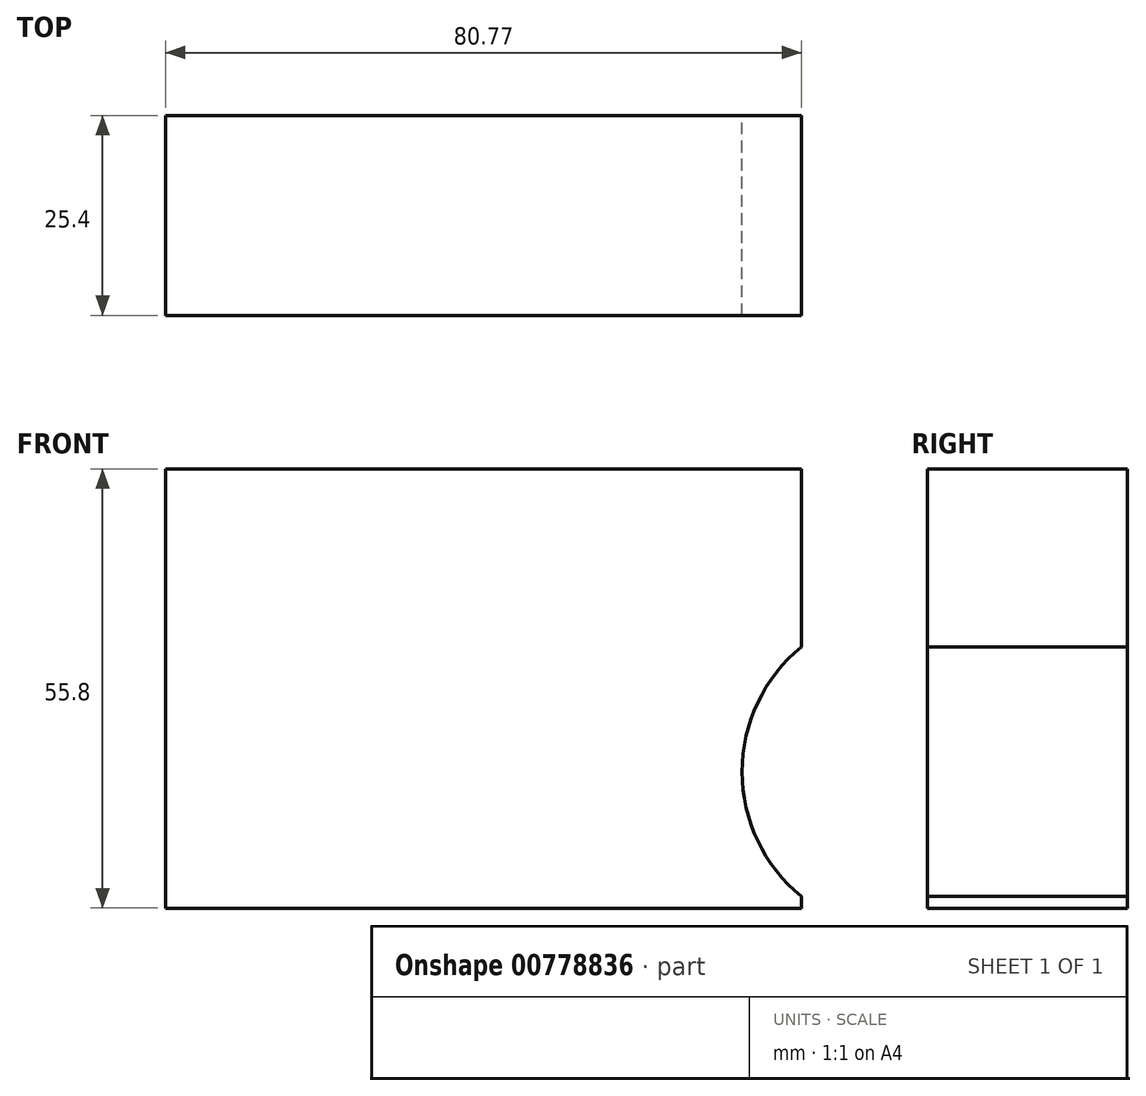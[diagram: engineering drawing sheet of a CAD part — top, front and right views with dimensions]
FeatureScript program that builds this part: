
annotation { "Feature Type Name" : "Feature", "Feature Type Description" : "" }
export const myFeature = defineFeature(function(context is Context, id is Id, definition is map)
    precondition{}
    {
        {
            var Q0;
            Q0=qCreatedBy(makeId("Front.planeOp"),FACE);
            var sketch = newSketch(context, id + "F0", { "sketchPlane" : qUnion([Q0])});
            skLineSegment(sketch, "E0.bottom", {"start": v(-116.45, 60.65) * mm, "end": v(-35.68, 60.65) * mm});
            skLineSegment(sketch, "E0.top", {"start": v(-116.45, 4.85) * mm, "end": v(-35.68, 4.85) * mm});
            skLineSegment(sketch, "E0.left", {"start": v(-116.45, 60.65) * mm, "end": v(-116.45, 4.85) * mm});
            skLineSegment(sketch, "E0.right", {"start": v(-35.68, 60.65) * mm, "end": v(-35.68, 4.85) * mm});
            skCircle(sketch, "E1", {"center": v(-22.76, 22.17) * mm, "radius": 20.45 * mm});
            skSolve(sketch);
        }
        {
            var Q0;
            {var subQ1=sQuery(id+"F0.wireOp",EDGE,"E0.bottom");Q0=makeQuery(id+"F0.imprint","IMPRINT",FACE,{"disambiguationData":[TD([[makeQuery(id+"F0.imprint","IMPRINT",EDGE,{"derivedFrom":subQ1}),-1.0]])]});}
            extrude(context, id + "F1", {"entities" : qUnion([Q0]), "depth" : 25.4 * mm, "offsetDistance" : 25.4 * mm});
        }
        {
            var Q0;
            {var subQ0=sQuery(id+"F0.wireOp",EDGE,"E1");var subQ1=sQuery(id+"F0.wireOp",EDGE,"E0.right");var subQ2=makeQuery(id+"F0.imprint","INTERSECT",VERTEX,{"disambiguationData":[OD(0.0)],"derivedFrom":[subQ1,subQ0]});Q0=makeQuery(id+"F0.imprint","IMPRINT",FACE,{"disambiguationData":[TD([[makeQuery(id+"F0.imprint","IMPRINT",EDGE,{"disambiguationData":[TD([[subQ2,-1.0]])],"derivedFrom":subQ1}),-1.0]])]});}
            var Q1;
            {var subQ0=sQuery(id+"F0.wireOp",EDGE,"E1");var subQ1=sQuery(id+"F0.wireOp",EDGE,"E0.right");var subQ2=makeQuery(id+"F0.imprint","INTERSECT",VERTEX,{"disambiguationData":[OD(0.0)],"derivedFrom":[subQ1,subQ0]});Q1=makeQuery(id+"F0.imprint","IMPRINT",FACE,{"disambiguationData":[TD([[makeQuery(id+"F0.imprint","IMPRINT",EDGE,{"disambiguationData":[TD([[subQ2,-1.0]])],"derivedFrom":subQ1}),1.0]])]});}
            extrude(context, id + "F2", {"entities" : qUnion([Q0, Q1]), "depth" : 25.4 * mm, "offsetDistance" : 25.4 * mm});
        }
    });
